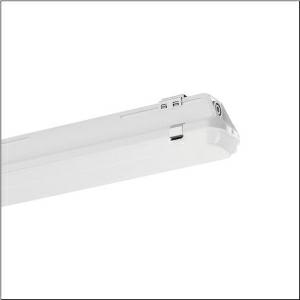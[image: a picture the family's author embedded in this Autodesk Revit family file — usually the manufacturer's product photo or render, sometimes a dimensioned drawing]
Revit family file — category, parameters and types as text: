
# Revit family: monsun_r__21_51fb107p480c_4b7a
name_source: partatom
category: Lighting Fixtures
units: mm (PartAtom-declared; Revit-internal decimal feet)

## family parameters
Cut with Voids When Loaded = No
Host = Face
Light Source = No
Part Type = Normal
Room Calculation Point = No
Round Connector Dimension = Use Diameter
Shared = No

## types (1)
- Monsun® 21 (1 x LED, 8070 lm, 44.5 W, 4000K)
    Apparent Load = 45 VA
    CIE Flux Codes = 47 77 93 94 100
    Color Rendering = 80
    Color Temperature = 4000K
    Default Elevation = 1800 mm
    Description = Monsun® 21, damp-proof luminaire, chain hanger, primary optical cover: enclosure, of PMMA, light emission: direct distribution, primary light characteristic: symmetric, installation type: suspended mounting, surface-mounted, horizontal mounting, vertical mounting, LED, rated luminous flux: 8.070lm, luminous efficacy: 181lm/W, light colour: 840, colour temperature: 4000K, control gear: ON/OFF, with terminal, 3-pole, max. 2.5mm², mains connection: 220..240V, AC, 50/60Hz, rated input power: 45W, housing, of glass-fibre reinforced polyester, uncoated, bright grey, incl. chain hanger, length: 1.590mm, width: 90mm, height: 88mm, clip for enclosure, of stainless steel (V2A), ceiling mounting element, of stainless steel (V2A), chain hanger, of stainless steel (V2A), protection rating (complete): IP66, insulation class (complete): insulation class I (protective earthing), certification: CE, ENEC, VDE, UKCA, protection symbol: D, impact resistance: IK04, permissible operating ambient temperature: -25..+35°C, standard: EN 50419, EN 60598-2-1, corresponds to IFS (International Featured Standards) requirements for safety and quality in the food industry, for indoor or canopied outdoor use, no direct snow, no direct sun, no direct rain, LABS conformity tested according to VDMA 24364:2018-05, contact your sales advisor before using the luminaires in applications with unclear chemical exposure, large temperature fluctuations or condensation-forming humidity, packaging unit: 1 piece
    Height = 89 mm
    Lamp = 1 x LED
    Lamp Light Flux = 8070 lm
    Lamp Power = 44.5 W
    Lamp count = 1
    Length = 1590 mm
    Luminous efficacy = 181 lm/W
    Manufacturer = Siteco
    ModVariant = No
    Model = 51FB107P480C
    Mounting Place = Ceiling
    Mounting Type = Surface mounted
    Number of Poles = 1
    OnlyDefault = Yes
    Power Factor = 1
    Product Name = Monsun® 21
    Product group = damp-proof luminaire
    ProductGroupID = 301
    Protection Class = Protection class I
    Protection Degree = IP 66
    RLX_Detail_Level = 1
    RLX_Emergency_Light_Flux = 0 lm
    RLX_Emergency_Type = 0
    RLX_Emergency_Type_DB = No
    RlxData = <blob elided: 88641 chars, md5=2d6e2b36>
    Socket = socket
    Standby Power = 0 W
    System Light Flux = 8070 lm
    System Power = 45 W
    Type Comments = Product without accessories
    Type Image = l_1319656.jpg
    URL = http://relux.com
    VarID = ---
    Voltage = 0 V
    Weight = 0.00 kg
    Width = 90 mm

## geometry (parser evidence)
native form markers: Blend x4, Sweep x12
no freeform markers — native parametric forms only
